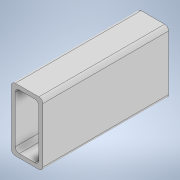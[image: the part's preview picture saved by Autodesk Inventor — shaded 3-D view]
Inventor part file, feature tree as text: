
AUTODESK INVENTOR PART (.ipt)
format: ipt  version: 2020 (Build 240168000, 168)  size: 117,248 bytes
history: native  units: in
note: dims shown in document units (in); Inventor stores cm internally (conversion verified against a paired STEP export)
features: extrude x1, sketch x1
ambient origin geometry x8: Origin, YZ Plane, XZ Plane, XY Plane, X Axis, Y Axis, Z Axis, Center Point
bodies: Solid1 (feature_tree)
feature tree (2):
  extrude  "Extrusion1"  Depth=1.0in
  sketch  "Sketch1"  dims[d0=2.0in d1=1.0in d2=0.125in d3=0.125in d4=0.125in d5=0.125in d6=0.125in d7=0.125in d8=0.125in d9=0.125in d10=0.125in d11=4.0in d12=0.0in]
